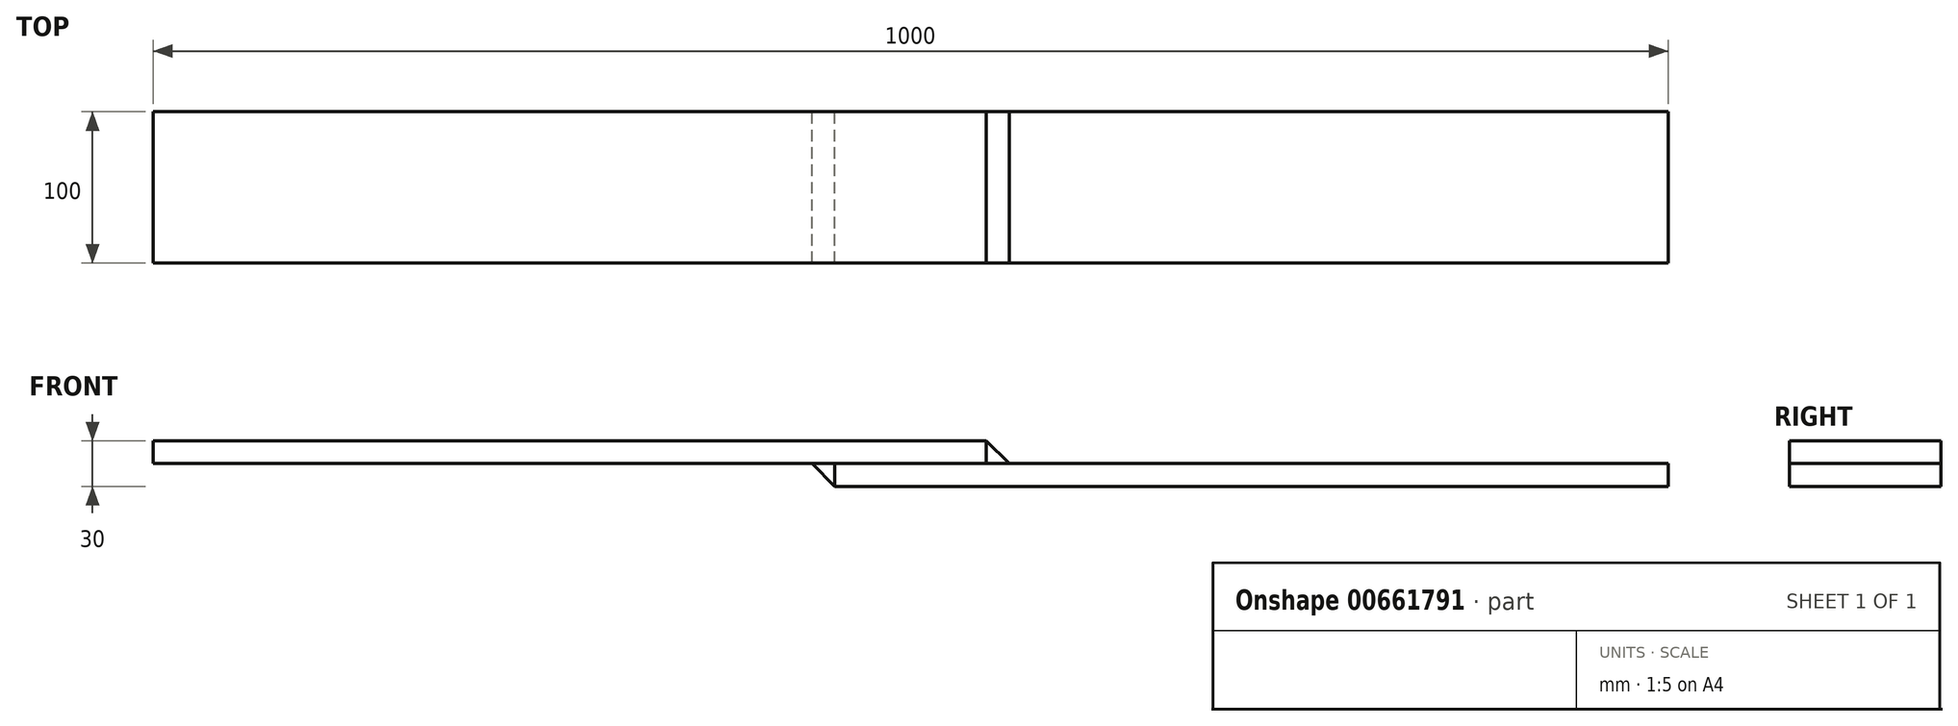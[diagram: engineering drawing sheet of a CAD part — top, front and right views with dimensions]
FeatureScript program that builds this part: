
annotation { "Feature Type Name" : "Feature", "Feature Type Description" : "" }
export const myFeature = defineFeature(function(context is Context, id is Id, definition is map)
    precondition{}
    {
        {
            assignVariable(context, id + "F0", {"name" : "W", "anyValue" : 100});
        }
        {
            var Q0;
            Q0=qCreatedBy(makeId("Front.planeOp"),FACE);
            var sketch = newSketch(context, id + "F1", { "sketchPlane" : qUnion([Q0])});
            skLineSegment(sketch, "E0.bottom", {"start": v(0, 0) * mm, "end": v(550, 0) * mm});
            skLineSegment(sketch, "E0.top", {"start": v(0, 15) * mm, "end": v(550, 15) * mm});
            skLineSegment(sketch, "E0.left", {"start": v(0, 0) * mm, "end": v(0, 15) * mm});
            skLineSegment(sketch, "E0.right", {"start": v(550, 0) * mm, "end": v(550, 15) * mm});
            skLineSegment(sketch, "E1.bottom", {"start": v(450, 0) * mm, "end": v(1000, 0) * mm});
            skLineSegment(sketch, "E1.top", {"start": v(450, -15) * mm, "end": v(1000, -15) * mm});
            skLineSegment(sketch, "E1.left", {"start": v(450, 0) * mm, "end": v(450, -15) * mm});
            skLineSegment(sketch, "E1.right", {"start": v(1000, 0) * mm, "end": v(1000, -15) * mm});
            skLineSegment(sketch, "E2", {"start": v(500, 49.52) * mm, "end": v(500, -50.18) * mm, "construction": true});
            skLineSegment(sketch, "E3", {"start": v(550, 15) * mm, "end": v(565, 0) * mm});
            skLineSegment(sketch, "E4", {"start": v(450, -15) * mm, "end": v(435, 0) * mm});
            skSolve(sketch);
        }
        {
            var Q0;
            Q0=makeQuery(id+"F1.imprint","IMPRINT",FACE,{"disambiguationData":[TD([[makeQuery(id+"F1.imprint","IMPRINT",EDGE,{"derivedFrom":sQuery(id+"F1.wireOp",EDGE,"E0.top")}),-1.0]])]});
            extrude(context, id + "F2", {"entities" : qUnion([Q0]), "depth" : (getVariable(context, 'W')) * mm, "offsetDistance" : 25 * mm});
        }
        {
            var Q0;
            Q0=makeQuery(id+"F1.imprint","IMPRINT",FACE,{"disambiguationData":[TD([[makeQuery(id+"F1.imprint","IMPRINT",EDGE,{"derivedFrom":sQuery(id+"F1.wireOp",EDGE,"E1.top")}),1.0]])]});
            extrude(context, id + "F3", {"entities" : qUnion([Q0]), "depth" : (getVariable(context, 'W')) * mm, "offsetDistance" : 25 * mm});
        }
        {
            var Q0;
            {var subQ0=sQuery(id+"F1.wireOp",EDGE,"E0.right");Q0=makeQuery(id+"F1.imprint","IMPRINT",FACE,{"disambiguationData":[TD([[makeQuery(id+"F1.imprint","IMPRINT",EDGE,{"derivedFrom":subQ0}),-1.0]])]});}
            extrude(context, id + "F4", {"entities" : qUnion([Q0]), "depth" : (getVariable(context, 'W')) * mm, "offsetDistance" : 25 * mm});
        }
        {
            var Q0;
            {var subQ0=sQuery(id+"F1.wireOp",EDGE,"E1.left");Q0=makeQuery(id+"F1.imprint","IMPRINT",FACE,{"disambiguationData":[TD([[makeQuery(id+"F1.imprint","IMPRINT",EDGE,{"derivedFrom":subQ0}),-1.0]])]});}
            extrude(context, id + "F5", {"entities" : qUnion([Q0]), "depth" : (getVariable(context, 'W')) * mm, "offsetDistance" : 25 * mm});
        }
    });
